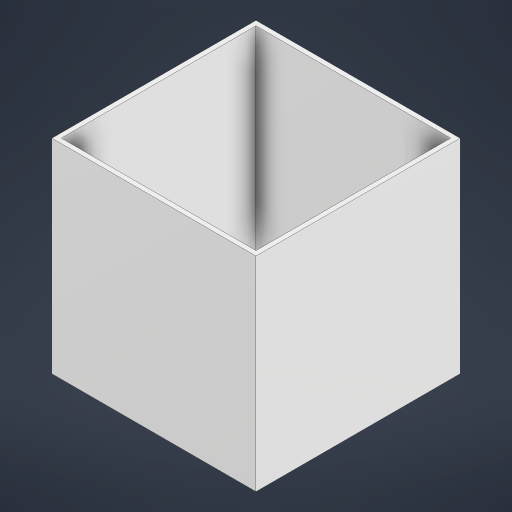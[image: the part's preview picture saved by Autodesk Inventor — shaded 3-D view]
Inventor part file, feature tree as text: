
AUTODESK INVENTOR PART (.ipt)
format: ipt  version: 2023 (Build 270158000, 158)  size: 162,816 bytes
history: native  units: mm
features: extrude x1, sketch x1
ambient origin geometry x8: Origin, YZ Plane, XZ Plane, XY Plane, X Axis, Y Axis, Z Axis, Center Point
bodies: Body1 (feature_tree)
feature tree (2):
  extrude  "Extrusion5"  Depth=54.0mm
  sketch  "Sketch2"  dims[d31=54.0mm d32=54.0mm d33=5.0mm d43=1.25mm d44=54.0mm d45=0.0mm]
